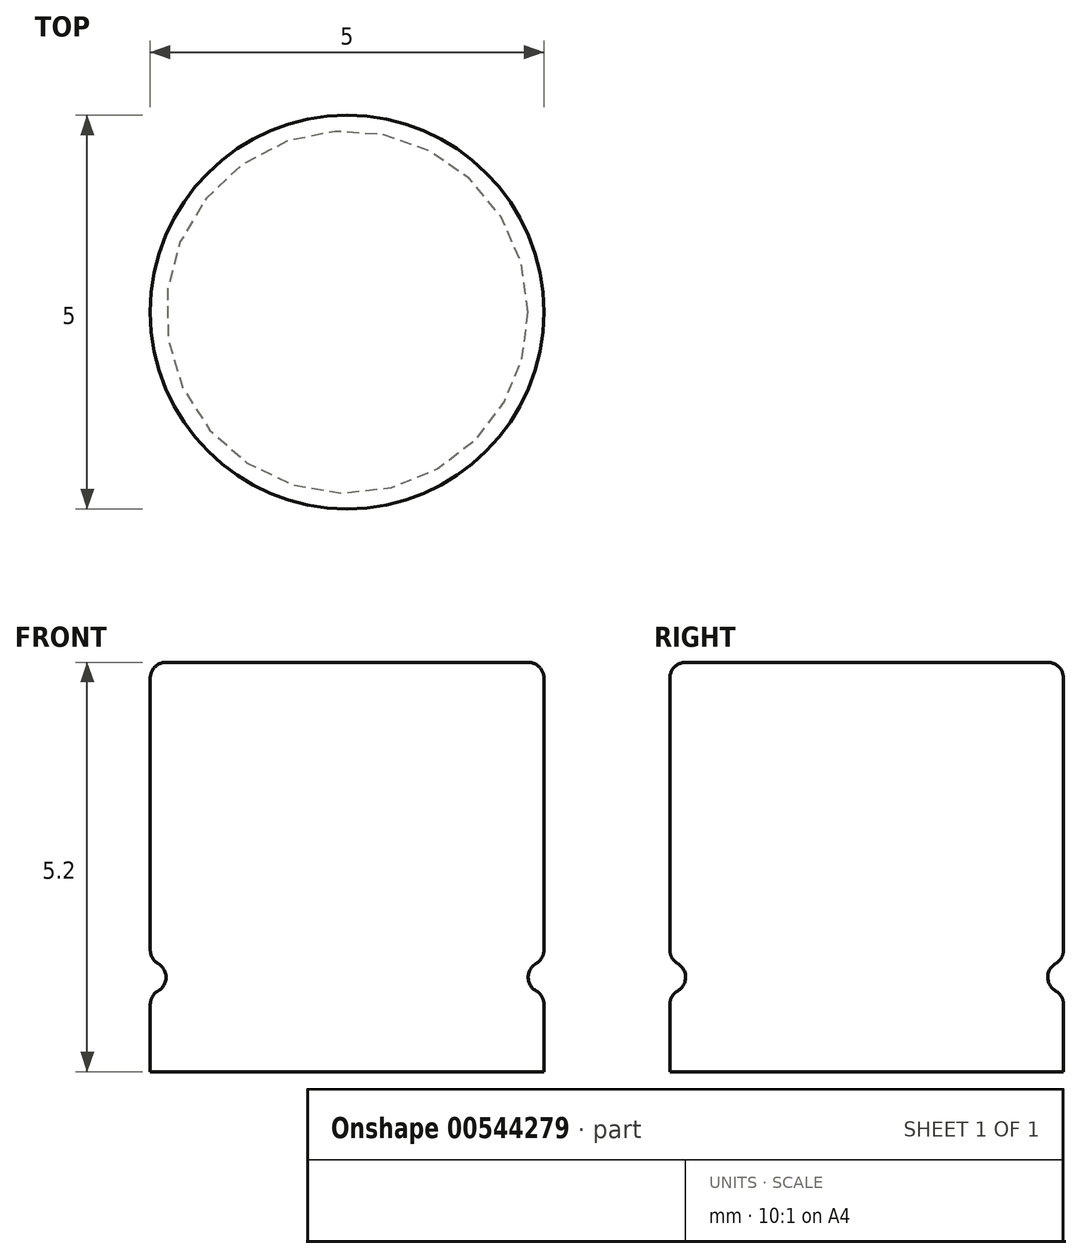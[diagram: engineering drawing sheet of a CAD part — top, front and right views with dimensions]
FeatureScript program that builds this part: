
annotation { "Feature Type Name" : "Feature", "Feature Type Description" : "" }
export const myFeature = defineFeature(function(context is Context, id is Id, definition is map)
    precondition{}
    {
        {
            var Q0;
            Q0=qCreatedBy(makeId("Front.planeOp"),FACE);
            var sketch = newSketch(context, id + "F0", { "sketchPlane" : qUnion([Q0])});
            skLineSegment(sketch, "E0.bottom", {"start": v(0, 5.2) * mm, "end": v(2.5, 5.2) * mm});
            skLineSegment(sketch, "E0.top", {"start": v(0, 0) * mm, "end": v(2.5, 0) * mm});
            skLineSegment(sketch, "E0.left", {"start": v(0, 5.2) * mm, "end": v(0, 0) * mm});
            skLineSegment(sketch, "E0.right", {"start": v(2.5, 5.2) * mm, "end": v(2.5, 1.4) * mm});
            skArc(sketch, "E1", {"start": v(2.5, 1.4) * mm, "mid": v(2.3, 1.2) * mm, "end": v(2.5, 1) * mm});
            skLineSegment(sketch, "E2.trimOffspring", {"start": v(2.5, 1) * mm, "end": v(2.5, 0) * mm});
            skLineSegment(sketch, "E3", {"start": v(0, 13.41) * mm, "end": v(0, 0) * mm, "construction": true});
            skSolve(sketch);
        }
        {
            var Q0;
            Q0=makeQuery(id+"F0.imprint","IMPRINT",FACE,{"disambiguationData":[TD([[makeQuery(id+"F0.imprint","IMPRINT",EDGE,{"derivedFrom":sQuery(id+"F0.wireOp",EDGE,"E0.bottom")}),-1.0]])]});
            var Q1;
            Q1=sQuery(id+"F0.wireOp",EDGE,"E3");
            revolve(context, id + "F1", {"entities" : qUnion([Q0]), "axis" : qUnion([Q1]), "revolveType" : RevolveType.FULL});
        }
        {
            var Q0;
            Q0=makeQuery(id+"F1.opRevolve","SWEPT_EDGE",EDGE,{"disambiguationData":[OSD([sQuery(id+"F0.wireOp",EDGE,"E0.right"),sQuery(id+"F0.wireOp",EDGE,"E1")])]});
            var Q1;
            Q1=makeQuery(id+"F1.opRevolve","SWEPT_EDGE",EDGE,{"disambiguationData":[OSD([sQuery(id+"F0.wireOp",EDGE,"E1"),sQuery(id+"F0.wireOp",EDGE,"E2.trimOffspring")])]});
            var Q2;
            Q2=makeQuery(id+"F1.opRevolve","SWEPT_EDGE",EDGE,{"disambiguationData":[OSD([sQuery(id+"F0.wireOp",EDGE,"E0.bottom"),sQuery(id+"F0.wireOp",EDGE,"E0.right")])]});
            fillet(context, id + "F2", {"entities" : qUnion([Q0, Q1, Q2]), "radius" : 0.2 * mm, "tangentPropagation" : true, "allowEdgeOverflow" : false});
        }
    });
